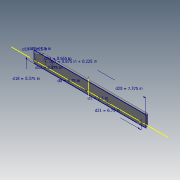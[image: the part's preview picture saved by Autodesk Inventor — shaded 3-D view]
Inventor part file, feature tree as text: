
AUTODESK INVENTOR PART (.ipt)
format: ipt  version: 2020.3 (Build 243373000, 373)  size: 151,552 bytes
history: native  units: in
note: dims shown in document units (in); Inventor stores cm internally (conversion verified against a paired STEP export)
features: sketch x3, extrude x2, hole x2, other x2, chamfer x1, fillet x1
ambient origin geometry x8: Origin, YZ Plane, XZ Plane, XY Plane, X Axis, Y Axis, Z Axis, Center Point
bodies: Solid1 (feature_tree)
feature tree (11):
  sketch  "Sketch1"  dims[d0=6.75in d1=2.5in d4=0.25in d5=0.0in]
  extrude  "Extrusion1"  Depth=2.5in
  sketch  "Sketch2"  dims[d13=1.0in d14=0.125in d15=0.1374in d16=0.125in]
  chamfer  "Chamfer1"  Distance=0.25in
  fillet  "Fillet1"  Radius=0.125in
  hole  "Hole2"  [1 undecoded]
  extrude  "Extrusion2"  Depth=0.25in
  other  "Work Axis1"
  other  "Work Axis2"
  hole  "Hole3"  [1 undecoded]
  sketch  "Sketch3"  dims[d17=1.1in d18=0.375in d19=0.25in d20=7.375in d21=6.75in d22=0.217in d23=0.75in d24=0.409in d25=0.25in d26=90.0deg d27=1.0in d28=0.8108in d29=0.1in d30=0.125in d31=1.0in d32=0.0in d33=0.875in d34=0.565in d35=1.5in d36=0.123in d37=0.75in d38=0.375in d39=0.25in d40=0.5635in d41=1.0in d42=0.8108in]
note: 2 required parameter values undecoded (feature->parameter linkage not recoverable at this tier; creation-order binding heuristic only, values carry confidence <= 0.55)
